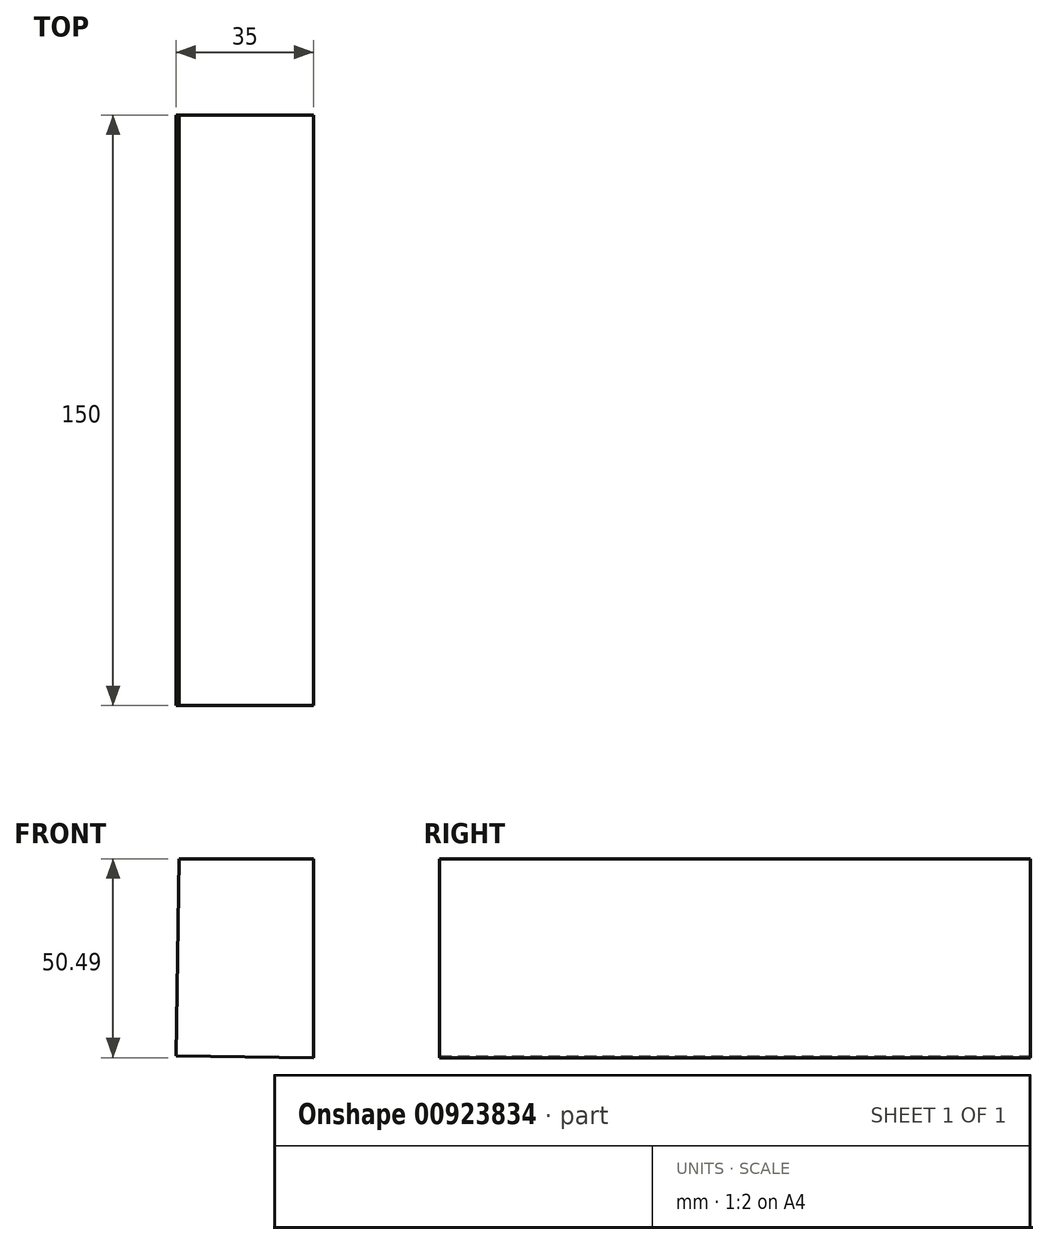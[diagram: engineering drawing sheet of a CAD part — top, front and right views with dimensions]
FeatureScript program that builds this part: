
annotation { "Feature Type Name" : "Feature", "Feature Type Description" : "" }
export const myFeature = defineFeature(function(context is Context, id is Id, definition is map)
    precondition{}
    {
        {
            var Q0;
            Q0=qCreatedBy(makeId("Front.planeOp"),FACE);
            var sketch = newSketch(context, id + "F0", { "sketchPlane" : qUnion([Q0])});
            skLineSegment(sketch, "E0", {"start": v(-249.54, -38.76) * mm, "end": v(-248.72, 11.24) * mm});
            skLineSegment(sketch, "E1", {"start": v(-248.72, 11.24) * mm, "end": v(-214.54, 11.24) * mm});
            skLineSegment(sketch, "E2", {"start": v(-214.54, 11.24) * mm, "end": v(-214.54, -39.25) * mm});
            skLineSegment(sketch, "E3", {"start": v(-214.54, -39.25) * mm, "end": v(-249.54, -38.76) * mm});
            skSolve(sketch);
        }
        {
            var Q0;
            Q0=makeQuery(id+"F0.imprint","IMPRINT",FACE,{"disambiguationData":[TD([[makeQuery(id+"F0.imprint","IMPRINT",EDGE,{"derivedFrom":sQuery(id+"F0.wireOp",EDGE,"E0")}),-1.0]])]});
            extrude(context, id + "F1", {"entities" : qUnion([Q0]), "depth" : 150 * mm, "offsetDistance" : 25 * mm});
        }
    });
